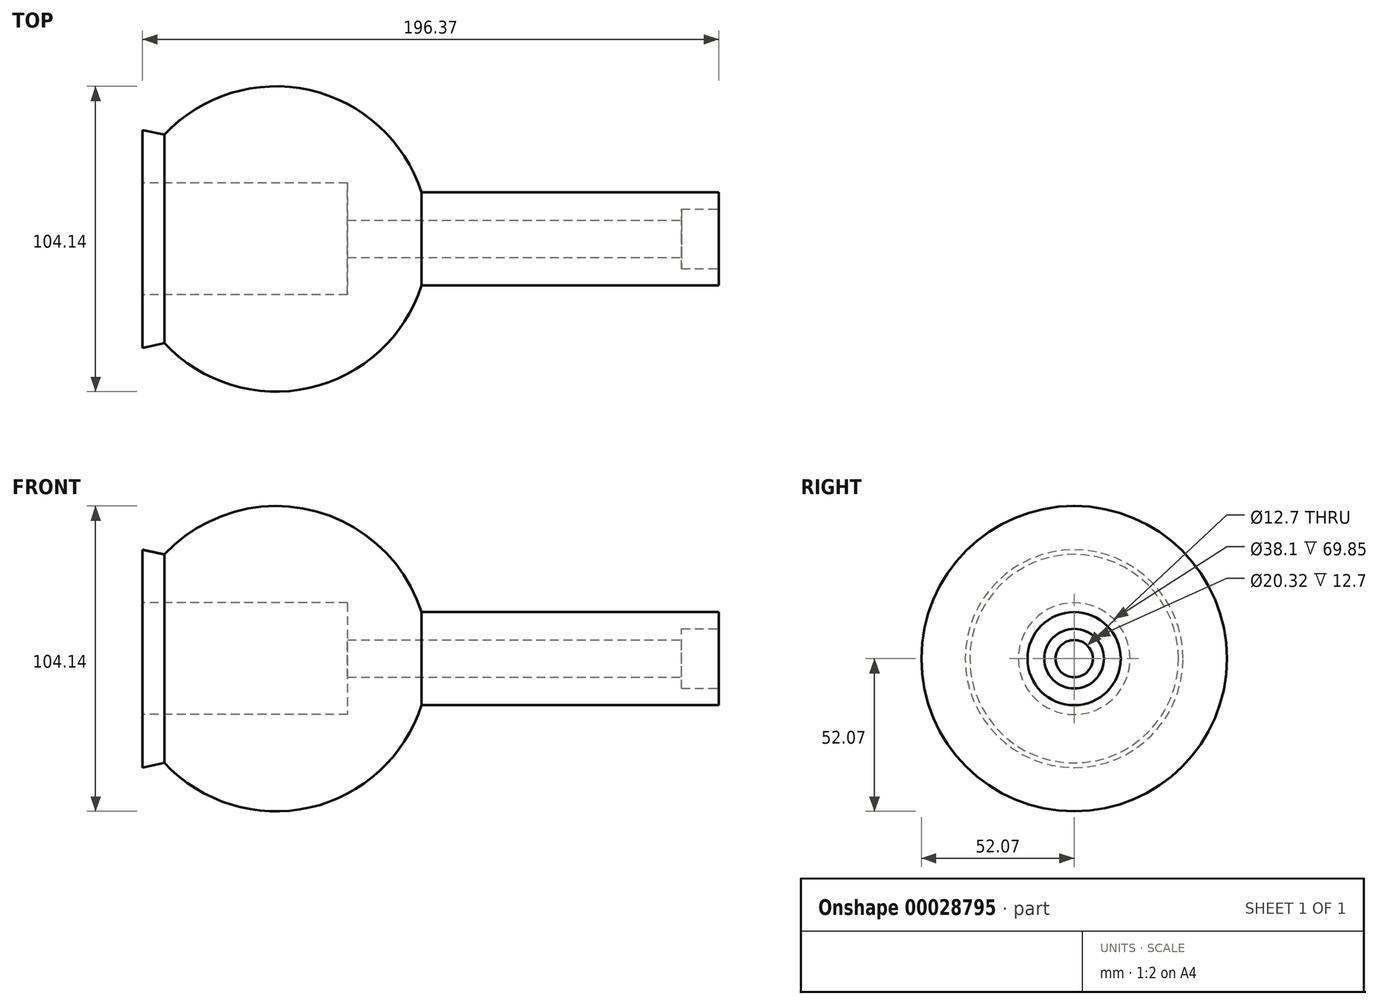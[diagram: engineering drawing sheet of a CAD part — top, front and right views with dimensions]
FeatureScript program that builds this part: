
annotation { "Feature Type Name" : "Feature", "Feature Type Description" : "" }
export const myFeature = defineFeature(function(context is Context, id is Id, definition is map)
    precondition{}
    {
        {
            var Q0;
            Q0=qCreatedBy(makeId("Front.planeOp"),FACE);
            var sketch = newSketch(context, id + "F0", { "sketchPlane" : qUnion([Q0])});
            skLineSegment(sketch, "E0", {"start": v(-53.76, 35.56) * mm, "end": v(65.53, 35.56) * mm, "construction": true});
            skLineSegment(sketch, "E1", {"start": v(-61.49, -35.56) * mm, "end": v(80.65, -35.56) * mm, "construction": true});
            skLineSegment(sketch, "E2", {"start": v(-25.4, 64.85) * mm, "end": v(-25.4, -82.76) * mm, "construction": true});
            skLineSegment(sketch, "E3", {"start": v(-26.35, 35.56) * mm, "end": v(-33.8, 37.14) * mm});
            skLineSegment(sketch, "E4", {"start": v(-33.8, 37.14) * mm, "end": v(-33.8, 0) * mm});
            skArc(sketch, "E5.trimOffspring", {"start": v(0.25, 50.8) * mm, "mid": v(0.13, 50.8) * mm, "end": v(0, 50.8) * mm});
            skLineSegment(sketch, "E6", {"start": v(0, 0) * mm, "end": v(-33.8, 0) * mm, "construction": true});
            skLineSegment(sketch, "E7", {"start": v(-33.8, 0) * mm, "end": v(63.75, 0) * mm});
            skArc(sketch, "E8.trimOffspring", {"start": v(63.75, 0) * mm, "mid": v(30.8, 48.43) * mm, "end": v(-26.35, 35.56) * mm});
            skSolve(sketch);
        }
        {
            var Q0;
            {var subQ2=sQuery(id+"F0.wireOp",EDGE,"E3");Q0=makeQuery(id+"F0.imprint","IMPRINT",FACE,{"disambiguationData":[TD([[makeQuery(id+"F0.imprint","IMPRINT",EDGE,{"derivedFrom":subQ2}),1.0]])]});}
            var Q1;
            Q1=sQuery(id+"F0.wireOp",EDGE,"E7");
            revolve(context, id + "F1", {"entities" : qUnion([Q0]), "axis" : qUnion([Q1]), "revolveType" : RevolveType.FULL});
        }
        {
            var Q0;
            Q0=makeQuery(id+"F1.opRevolve","SWEPT_FACE",FACE,{"disambiguationData":[OSD([sQuery(id+"F0.wireOp",EDGE,"E4")])]});
            var sketch = newSketch(context, id + "F2", { "sketchPlane" : qUnion([Q0])});
            skCircle(sketch, "E9", {"center": v(0, 0) * mm, "radius": 19.05 * mm});
            skSolve(sketch);
        }
        {
            var Q0;
            Q0=makeQuery(id+"F2.imprint","IMPRINT",FACE,{"disambiguationData":[TD([[makeQuery(id+"F2.imprint","IMPRINT",EDGE,{"derivedFrom":sQuery(id+"F2.wireOp",EDGE,"E9")}),1.0]])]});
            extrude(context, id + "F3", {"entities" : qUnion([Q0]), "operationType" : NewBodyOperationType.REMOVE, "oppositeDirection" : true, "depth" : 69.85 * mm});
        }
        {
            var Q0;
            Q0=qCreatedBy(makeId("Right.planeOp"),FACE);
            cPlane(context, id + "F4", {"entities" : qUnion([Q0]), "cplaneType" : CPlaneType.OFFSET, "offset" : 60.96 * mm, "width" : 152.4 * mm, "height" : 152.4 * mm});
        }
        {
            var Q0;
            Q0=qCreatedBy(id+"F4.planeOp",FACE);
            var sketch = newSketch(context, id + "F5", { "sketchPlane" : qUnion([Q0])});
            skCircle(sketch, "E10", {"center": v(0, 0) * mm, "radius": 15.88 * mm});
            skSolve(sketch);
        }
        {
            var Q0;
            Q0=makeQuery(id+"F5.imprint","IMPRINT",FACE,{"disambiguationData":[TD([[makeQuery(id+"F5.imprint","IMPRINT",EDGE,{"derivedFrom":sQuery(id+"F5.wireOp",EDGE,"E10")}),1.0]])]});
            extrude(context, id + "F6", {"entities" : qUnion([Q0]), "operationType" : NewBodyOperationType.ADD, "depth" : 101.6 * mm});
        }
        {
            var Q0;
            Q0=makeQuery(id+"F6.opExtrude","CAP_FACE",FACE,{"disambiguationData":[OSD([sQuery(id+"F5.wireOp",EDGE,"E10")])],"isStart":false});
            var sketch = newSketch(context, id + "F7", { "sketchPlane" : qUnion([Q0])});
            skCircle(sketch, "E11", {"center": v(0, 0) * mm, "radius": 6.35 * mm});
            skSolve(sketch);
        }
        {
            var Q0;
            Q0=makeQuery(id+"F7.imprint","IMPRINT",FACE,{"disambiguationData":[TD([[makeQuery(id+"F7.imprint","IMPRINT",EDGE,{"derivedFrom":sQuery(id+"F7.wireOp",EDGE,"E11")}),1.0]])]});
            extrude(context, id + "F8", {"entities" : qUnion([Q0]), "operationType" : NewBodyOperationType.REMOVE, "oppositeDirection" : true, "depth" : 209.95 * mm});
        }
        {
            var Q0;
            Q0=makeQuery(id+"F6.opExtrude","CAP_FACE",FACE,{"disambiguationData":[OSD([sQuery(id+"F5.wireOp",EDGE,"E10")])],"isStart":false});
            var sketch = newSketch(context, id + "F9", { "sketchPlane" : qUnion([Q0])});
            skCircle(sketch, "E12", {"center": v(0, 0) * mm, "radius": 10.16 * mm});
            skSolve(sketch);
        }
        {
            var Q0;
            Q0=makeQuery(id+"F9.imprint","IMPRINT",FACE,{"disambiguationData":[TD([[makeQuery(id+"F9.imprint","IMPRINT",EDGE,{"derivedFrom":sQuery(id+"F9.wireOp",EDGE,"E12")}),1.0]])]});
            extrude(context, id + "F10", {"entities" : qUnion([Q0]), "operationType" : NewBodyOperationType.REMOVE, "oppositeDirection" : true, "depth" : 12.7 * mm});
        }
    });
